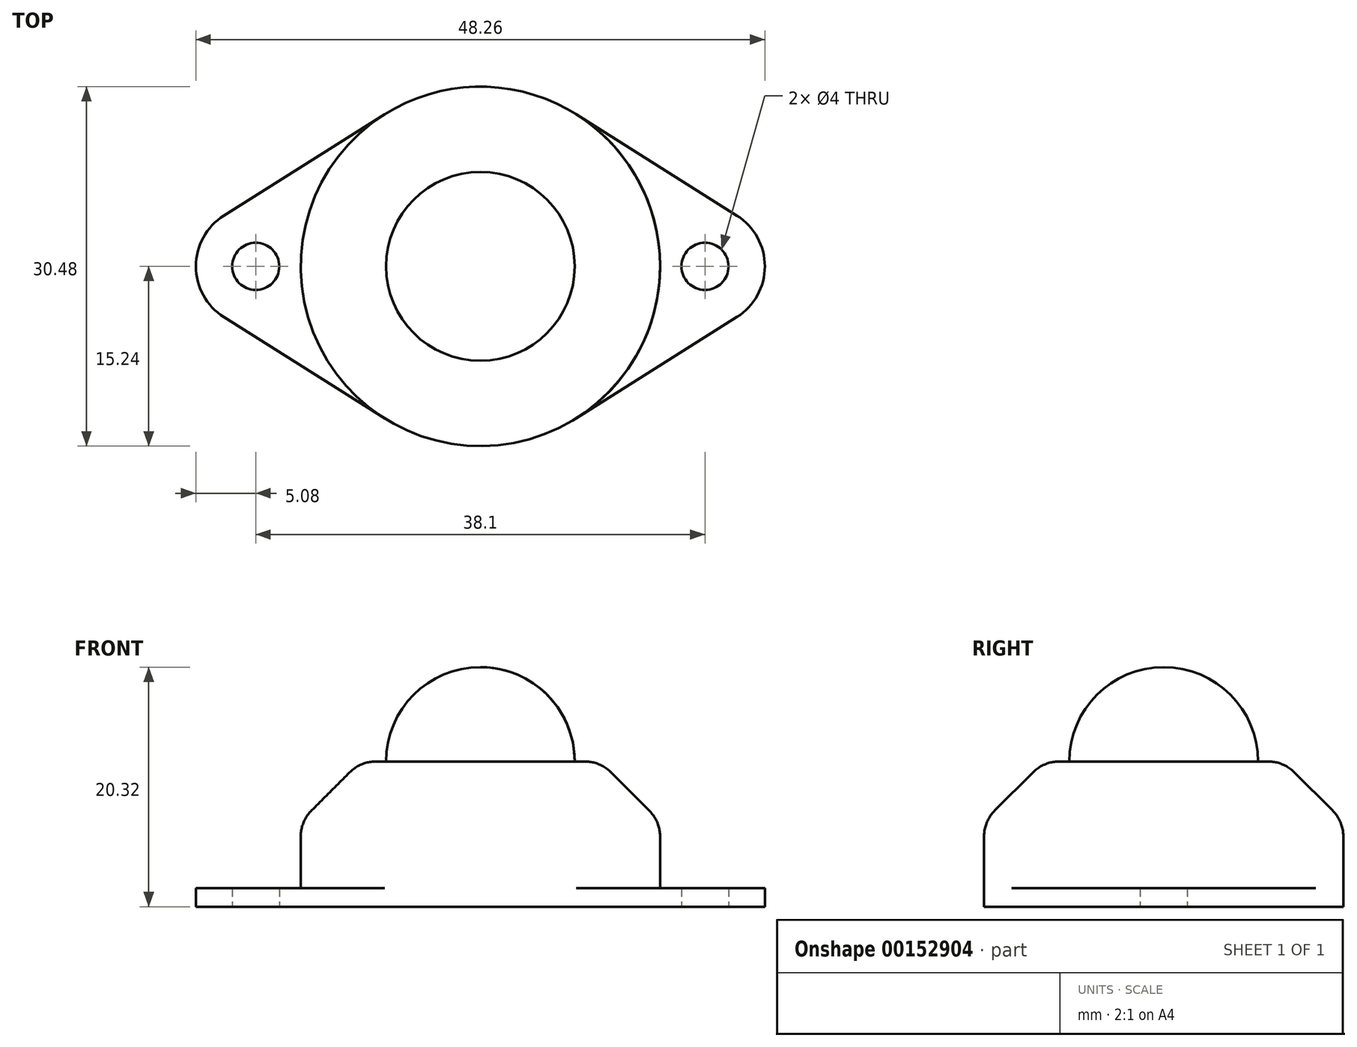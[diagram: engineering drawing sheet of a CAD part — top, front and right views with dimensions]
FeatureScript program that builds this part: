
annotation { "Feature Type Name" : "Feature", "Feature Type Description" : "" }
export const myFeature = defineFeature(function(context is Context, id is Id, definition is map)
    precondition{}
    {
        {
            var Q0;
            Q0=qCreatedBy(makeId("Top.planeOp"),FACE);
            var sketch = newSketch(context, id + "F0", { "sketchPlane" : qUnion([Q0])});
            skLineSegment(sketch, "E0", {"start": v(0, 0) * mm, "end": v(38.1, 0) * mm, "construction": true});
            skCircle(sketch, "E1", {"center": v(0, 0) * mm, "radius": 2 * mm});
            skCircle(sketch, "E2", {"center": v(38.1, 0) * mm, "radius": 2 * mm});
            skArc(sketch, "E3", {"start": v(-2.7, 4.3) * mm, "mid": v(-5.08, 0) * mm, "end": v(-2.7, -4.3) * mm});
            skArc(sketch, "E4", {"start": v(40.8, -4.3) * mm, "mid": v(43.18, 0) * mm, "end": v(40.8, 4.3) * mm});
            skArc(sketch, "E5", {"start": v(27.18, 12.9) * mm, "mid": v(19.05, 15.24) * mm, "end": v(10.92, 12.9) * mm});
            skArc(sketch, "E6", {"start": v(10.92, -12.9) * mm, "mid": v(19.05, -15.24) * mm, "end": v(27.18, -12.9) * mm});
            skLineSegment(sketch, "E7", {"start": v(-2.7, -4.3) * mm, "end": v(10.92, -12.9) * mm});
            skLineSegment(sketch, "E8", {"start": v(27.18, -12.9) * mm, "end": v(40.8, -4.3) * mm});
            skLineSegment(sketch, "E9", {"start": v(40.8, 4.3) * mm, "end": v(27.18, 12.9) * mm});
            skLineSegment(sketch, "E10", {"start": v(10.92, 12.9) * mm, "end": v(-2.7, 4.3) * mm});
            skSolve(sketch);
        }
        {
            var Q0;
            Q0 = qSketchRegion(id + "F0", true);
            extrude(context, id + "F1", {"entities" : qUnion([Q0]), "depth" : 1.59 * mm});
        }
        {
            var Q0;
            Q0=makeQuery(id+"F1.opExtrude","CAP_FACE",FACE,{"disambiguationData":[OSD([sQuery(id+"F0.wireOp",EDGE,"E1"),sQuery(id+"F0.wireOp",EDGE,"E2"),sQuery(id+"F0.wireOp",EDGE,"E3"),sQuery(id+"F0.wireOp",EDGE,"E4"),sQuery(id+"F0.wireOp",EDGE,"E5"),sQuery(id+"F0.wireOp",EDGE,"E6"),sQuery(id+"F0.wireOp",EDGE,"E7"),sQuery(id+"F0.wireOp",EDGE,"E8"),sQuery(id+"F0.wireOp",EDGE,"E9"),sQuery(id+"F0.wireOp",EDGE,"E10")])],"isStart":false});
            var sketch = newSketch(context, id + "F2", { "sketchPlane" : qUnion([Q0])});
            skCircle(sketch, "E11", {"center": v(19.05, 0) * mm, "radius": 15.24 * mm});
            skSolve(sketch);
        }
        {
            var Q0;
            Q0 = qSketchRegion(id + "F2", true);
            extrude(context, id + "F3", {"entities" : qUnion([Q0]), "operationType" : NewBodyOperationType.ADD, "depth" : 10.73 * mm});
        }
        {
            var Q0;
            Q0=makeQuery(id+"F3.opExtrude","CAP_FACE",FACE,{"disambiguationData":[OSD([sQuery(id+"F2.wireOp",EDGE,"E11")])],"isStart":false});
            var sketch = newSketch(context, id + "F4", { "sketchPlane" : qUnion([Q0])});
            skCircle(sketch, "E12", {"center": v(19.05, 0) * mm, "radius": 8 * mm});
            skSolve(sketch);
        }
        {
            var Q0;
            Q0 = qSketchRegion(id + "F4", true);
            extrude(context, id + "F5", {"entities" : qUnion([Q0]), "operationType" : NewBodyOperationType.ADD, "depth" : 8 * mm});
        }
        {
            var Q0;
            Q0=makeQuery(id+"F5.opExtrude","CAP_EDGE",EDGE,{"disambiguationData":[OSD([sQuery(id+"F4.wireOp",EDGE,"E12")])],"isStart":false});
            fillet(context, id + "F6", {"entities" : qUnion([Q0]), "radius" : 8 * mm, "tangentPropagation" : true, "allowEdgeOverflow" : false});
        }
        {
            var Q0;
            Q0=makeQuery(id+"F3.opExtrude","CAP_EDGE",EDGE,{"disambiguationData":[OSD([sQuery(id+"F2.wireOp",EDGE,"E11")])],"isStart":false});
            chamfer(context, id + "F7", {"entities" : qUnion([Q0]), "width" : 5.08 * mm, "tangentPropagation" : true});
        }
        {
            var Q0;
            {var subQ0=sQuery(id+"F2.wireOp",EDGE,"E11");Q0=makeQuery(id+"F7.opChamfer","BLEND_EDGE",EDGE,{"blendedFrom":[makeQuery(id+"F3.opExtrude","CAP_EDGE",EDGE,{"disambiguationData":[OSD([subQ0])],"isStart":false}),makeQuery(id+"F3.boolean.opBoolean","MERGE",FACE,{"derivedFrom":[makeQuery(id+"F1.opExtrude","SWEPT_FACE",FACE,{"disambiguationData":[OSD([sQuery(id+"F0.wireOp",EDGE,"E5")])]}),makeQuery(id+"F1.opExtrude","SWEPT_FACE",FACE,{"disambiguationData":[OSD([sQuery(id+"F0.wireOp",EDGE,"E6")])]}),makeQuery(id+"F3.opExtrude","SWEPT_FACE",FACE,{"disambiguationData":[OSD([subQ0])]})]})],"blendedInto":[makeQuery(id+"F3.boolean.opBoolean","MERGE",FACE,{"derivedFrom":[makeQuery(id+"F1.opExtrude","SWEPT_FACE",FACE,{"disambiguationData":[OSD([sQuery(id+"F0.wireOp",EDGE,"E5")])]}),makeQuery(id+"F1.opExtrude","SWEPT_FACE",FACE,{"disambiguationData":[OSD([sQuery(id+"F0.wireOp",EDGE,"E6")])]}),makeQuery(id+"F3.opExtrude","SWEPT_FACE",FACE,{"disambiguationData":[OSD([subQ0])]})]})]});}
            var Q1;
            {var subQ0=sQuery(id+"F2.wireOp",EDGE,"E11");Q1=makeQuery(id+"F7.opChamfer","BLEND_EDGE",EDGE,{"blendedFrom":[makeQuery(id+"F3.opExtrude","CAP_EDGE",EDGE,{"disambiguationData":[OSD([subQ0])],"isStart":false}),makeQuery(id+"F3.opExtrude","CAP_FACE",FACE,{"disambiguationData":[OSD([subQ0])],"isStart":false})],"blendedInto":[makeQuery(id+"F3.opExtrude","CAP_FACE",FACE,{"disambiguationData":[OSD([subQ0])],"isStart":false})]});}
            fillet(context, id + "F8", {"entities" : qUnion([Q0, Q1]), "radius" : 3.17 * mm, "tangentPropagation" : true, "allowEdgeOverflow" : false});
        }
    });
